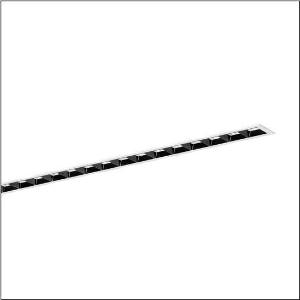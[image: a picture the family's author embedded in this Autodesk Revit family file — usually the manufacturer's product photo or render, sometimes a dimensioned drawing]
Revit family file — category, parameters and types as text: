
# Revit family: silica_r__21_51mx14da34wb_b271
name_source: partatom
category: Lighting Fixtures
units: mm (PartAtom-declared; Revit-internal decimal feet)

## family parameters
Cut with Voids When Loaded = No
Host = Face
Light Source = No
Part Type = Normal
Room Calculation Point = No
Round Connector Dimension = Use Diameter
Shared = No

## types (1)
- --- (1 x LED, 4320 lm, 32.1 W, 3000K)
    Apparent Load = 32 VA
    CIE Flux Codes = 74 94 99 100 100
    Color Rendering = 80
    Color Temperature = 3000K
    Default Elevation = 1800 mm
    Description = Silica® 21, office luminaire, primary light control with darklight reflector, of PMMA, black, light emission: direct distribution, primary light characteristic: asymmetric, installation type: recessed, LED, rated luminous flux: 4.320lm, luminous efficacy: 135lm/W, light colour: 830, colour temperature: 3000K, with terminal, 3+2-pole, max. 2.5mm², mains connection: 220..240V, AC, 50/60Hz, rated input power: 32.1W, luminaire housing, of aluminium, traffic white (RAL 9016), length: 1.228mm, width: 79mm, height: 53mm, protection rating (complete): IP20, insulation class (complete): insulation class I (protective earthing), certification: CE, permissible operating ambient temperature: 0..+35°C, standard: EN 50419, packaging unit: 1 piece
    Height = 0 mm  [stored 0 ft]
    Lamp = 1 x LED
    Lamp Light Flux = 4320 lm
    Lamp Power = 32.1 W
    Lamp count = 1
    Length = 1227 mm
    Luminous efficacy = 135 lm/W
    Manufacturer = Siteco
    ModVariant = No
    Model = 51MX14DA34WB
    Mounting Place = Ceiling
    Mounting Type = Recessed
    Number of Poles = 1
    OnlyDefault = Yes
    Power Factor = 1
    Product Name = Silica® 21
    Product group = office luminaire | ceiling recessed
    ProductGroupID = 401
    Protection Class = Protection class I
    Protection Degree = IP 20
    RLX_Detail_Level = 1
    RLX_Emergency_Light_Flux = 0 lm
    RLX_Emergency_Type = 0
    RLX_Emergency_Type_DB = No
    RlxData = <blob elided: 40417 chars, md5=8d41d539>
    Socket = socket
    Standby Power = 0 W
    System Light Flux = 4320 lm
    System Power = 32 W
    Type Comments = factory setting: luminous flux: 100 % | dim-lin: 254 | 448 mA
    Type Image = l_1297791.jpg
    URL = http://relux.com
    VarID = @adj_053183
    Voltage = 0 V
    Weight = 0.00 kg
    Width = 79 mm

note: [stored X ft] marks values corroborated as IEEE doubles in the binary element streams (Revit-internal decimal feet)

## geometry (parser evidence)
native form markers: Blend x4, Sweep x9
no freeform markers — native parametric forms only
